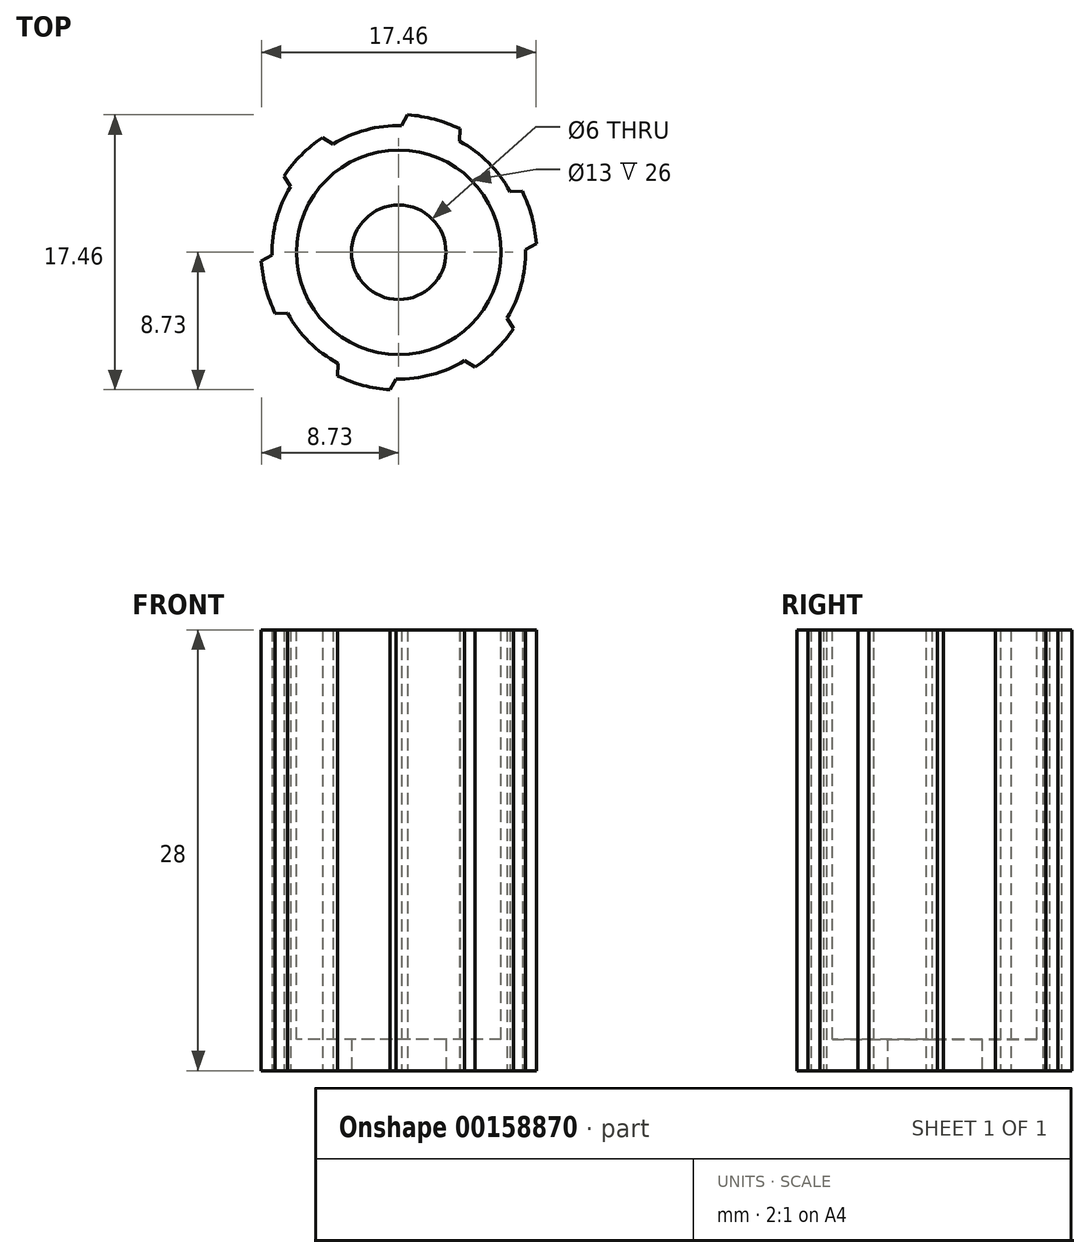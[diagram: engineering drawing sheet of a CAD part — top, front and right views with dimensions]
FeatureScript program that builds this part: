
annotation { "Feature Type Name" : "Feature", "Feature Type Description" : "" }
export const myFeature = defineFeature(function(context is Context, id is Id, definition is map)
    precondition{}
    {
        {
            var Q0;
            Q0=qCreatedBy(makeId("Top.planeOp"),FACE);
            var sketch = newSketch(context, id + "F0", { "sketchPlane" : qUnion([Q0])});
            skArc(sketch, "E0", {"start": v(6.97, -4.03) * mm, "mid": v(7.78, -2.08) * mm, "end": v(8.05, 0) * mm});
            skCircle(sketch, "E1", {"center": v(0, 0) * mm, "radius": 3 * mm});
            skArc(sketch, "E2", {"start": v(4.37, -7.58) * mm, "mid": v(6.19, -6.19) * mm, "end": v(7.58, -4.38) * mm});
            skLineSegment(sketch, "E3", {"start": v(0, -8.75) * mm, "end": v(0, -8.05) * mm});
            skLineSegment(sketch, "E4.1.0", {"start": v(4.37, -7.58) * mm, "end": v(4.03, -6.97) * mm});
            skLineSegment(sketch, "E4.2.0", {"start": v(7.58, -4.38) * mm, "end": v(6.97, -4.03) * mm});
            skLineSegment(sketch, "E4.3.0", {"start": v(8.75, 0) * mm, "end": v(8.05, 0) * mm});
            skLineSegment(sketch, "E4.4.0", {"start": v(7.58, 4.37) * mm, "end": v(6.97, 4.02) * mm});
            skLineSegment(sketch, "E4.5.0", {"start": v(4.37, 7.58) * mm, "end": v(4.03, 6.97) * mm});
            skLineSegment(sketch, "E4.6.0", {"start": v(0, 8.75) * mm, "end": v(0, 8.05) * mm});
            skLineSegment(sketch, "E4.7.0", {"start": v(-4.37, 7.58) * mm, "end": v(-4.02, 6.97) * mm});
            skLineSegment(sketch, "E4.8.0", {"start": v(-7.58, 4.38) * mm, "end": v(-6.97, 4.03) * mm});
            skLineSegment(sketch, "E4.9.0", {"start": v(-8.75, 0) * mm, "end": v(-8.05, 0) * mm});
            skLineSegment(sketch, "E4.10.0", {"start": v(-7.58, -4.38) * mm, "end": v(-6.97, -4.03) * mm});
            skLineSegment(sketch, "E4.11.0", {"start": v(-4.38, -7.58) * mm, "end": v(-4.03, -6.97) * mm});
            skArc(sketch, "E5.trimOffspring", {"start": v(8.75, 0) * mm, "mid": v(8.45, 2.26) * mm, "end": v(7.58, 4.37) * mm});
            skArc(sketch, "E6.trimOffspring", {"start": v(6.97, 4.02) * mm, "mid": v(5.7, 5.7) * mm, "end": v(4.02, 6.97) * mm});
            skArc(sketch, "E7.trimOffspring", {"start": v(4.38, 7.58) * mm, "mid": v(2.26, 8.45) * mm, "end": v(0, 8.75) * mm});
            skArc(sketch, "E8.trimOffspring", {"start": v(0, 8.05) * mm, "mid": v(-2.08, 7.78) * mm, "end": v(-4.02, 6.97) * mm});
            skArc(sketch, "E9.trimOffspring", {"start": v(-4.37, 7.58) * mm, "mid": v(-6.19, 6.19) * mm, "end": v(-7.58, 4.38) * mm});
            skArc(sketch, "E10.trimOffspring", {"start": v(-6.97, 4.02) * mm, "mid": v(-7.78, 2.08) * mm, "end": v(-8.05, 0) * mm});
            skArc(sketch, "E11.trimOffspring", {"start": v(-8.75, 0) * mm, "mid": v(-8.45, -2.26) * mm, "end": v(-7.58, -4.37) * mm});
            skArc(sketch, "E12.trimOffspring", {"start": v(-6.97, -4.03) * mm, "mid": v(-5.7, -5.7) * mm, "end": v(-4.03, -6.97) * mm});
            skArc(sketch, "E13.trimOffspring", {"start": v(-4.37, -7.58) * mm, "mid": v(-2.26, -8.45) * mm, "end": v(0, -8.75) * mm});
            skArc(sketch, "E14.trimOffspring", {"start": v(0, -8.05) * mm, "mid": v(2.08, -7.78) * mm, "end": v(4.02, -6.97) * mm});
            skSolve(sketch);
        }
        {
            var Q0;
            Q0 = qSketchRegion(id + "F0", true);
            extrude(context, id + "F1", {"entities" : qUnion([Q0]), "depth" : 28 * mm});
        }
        {
            var Q0;
            Q0=makeQuery(id+"F1.opExtrude","CAP_FACE",FACE,{"disambiguationData":[OSD([sQuery(id+"F0.wireOp",EDGE,"E0")])],"isStart":false});
            var sketch = newSketch(context, id + "F2", { "sketchPlane" : qUnion([Q0])});
            skCircle(sketch, "E15", {"center": v(0, 0) * mm, "radius": 6.5 * mm});
            skSolve(sketch);
        }
        {
            var Q0;
            Q0 = qSketchRegion(id + "F2", true);
            extrude(context, id + "F3", {"entities" : qUnion([Q0]), "operationType" : NewBodyOperationType.REMOVE, "oppositeDirection" : true, "depth" : 26 * mm});
        }
        {
            var Q0;
            Q0=makeQuery(id+"F1.opExtrude","SWEPT_EDGE",EDGE,{"disambiguationData":[OSD([sQuery(id+"F0.wireOp",EDGE,"E4.10.0"),sQuery(id+"F0.wireOp",EDGE,"E11.trimOffspring")])]});
            var Q1;
            Q1=makeQuery(id+"F1.opExtrude","SWEPT_EDGE",EDGE,{"disambiguationData":[OSD([sQuery(id+"F0.wireOp",EDGE,"E3"),sQuery(id+"F0.wireOp",EDGE,"E13.trimOffspring")])]});
            var Q2;
            Q2=makeQuery(id+"F1.opExtrude","SWEPT_EDGE",EDGE,{"disambiguationData":[OSD([sQuery(id+"F0.wireOp",EDGE,"E2"),sQuery(id+"F0.wireOp",EDGE,"E4.2.0")])]});
            var Q3;
            Q3=makeQuery(id+"F1.opExtrude","SWEPT_EDGE",EDGE,{"disambiguationData":[OSD([sQuery(id+"F0.wireOp",EDGE,"E4.4.0"),sQuery(id+"F0.wireOp",EDGE,"E5.trimOffspring")])]});
            var Q4;
            Q4=makeQuery(id+"F1.opExtrude","SWEPT_EDGE",EDGE,{"disambiguationData":[OSD([sQuery(id+"F0.wireOp",EDGE,"E4.6.0"),sQuery(id+"F0.wireOp",EDGE,"E7.trimOffspring")])]});
            var Q5;
            Q5=makeQuery(id+"F1.opExtrude","SWEPT_EDGE",EDGE,{"disambiguationData":[OSD([sQuery(id+"F0.wireOp",EDGE,"E4.8.0"),sQuery(id+"F0.wireOp",EDGE,"E9.trimOffspring")])]});
            chamfer(context, id + "F4", {"entities" : qUnion([Q0, Q1, Q2, Q3, Q4, Q5]), "chamferType" : ChamferType.TWO_OFFSETS, "width1" : 1 * mm, "oppositeDirection" : false, "width2" : 0.5 * mm, "tangentPropagation" : true});
        }
        {
            var Q0;
            Q0=makeQuery(id+"F1.opExtrude","SWEPT_EDGE",EDGE,{"disambiguationData":[OSD([sQuery(id+"F0.wireOp",EDGE,"E4.9.0"),sQuery(id+"F0.wireOp",EDGE,"E11.trimOffspring")])]});
            var Q1;
            Q1=makeQuery(id+"F1.opExtrude","SWEPT_EDGE",EDGE,{"disambiguationData":[OSD([sQuery(id+"F0.wireOp",EDGE,"E4.7.0"),sQuery(id+"F0.wireOp",EDGE,"E9.trimOffspring")])]});
            var Q2;
            Q2=makeQuery(id+"F1.opExtrude","SWEPT_EDGE",EDGE,{"disambiguationData":[OSD([sQuery(id+"F0.wireOp",EDGE,"E4.5.0"),sQuery(id+"F0.wireOp",EDGE,"E7.trimOffspring")])]});
            var Q3;
            Q3=makeQuery(id+"F1.opExtrude","SWEPT_EDGE",EDGE,{"disambiguationData":[OSD([sQuery(id+"F0.wireOp",EDGE,"E4.3.0"),sQuery(id+"F0.wireOp",EDGE,"E5.trimOffspring")])]});
            var Q4;
            Q4=makeQuery(id+"F1.opExtrude","SWEPT_EDGE",EDGE,{"disambiguationData":[OSD([sQuery(id+"F0.wireOp",EDGE,"E2"),sQuery(id+"F0.wireOp",EDGE,"E4.1.0")])]});
            var Q5;
            Q5=makeQuery(id+"F1.opExtrude","SWEPT_EDGE",EDGE,{"disambiguationData":[OSD([sQuery(id+"F0.wireOp",EDGE,"E4.11.0"),sQuery(id+"F0.wireOp",EDGE,"E13.trimOffspring")])]});
            chamfer(context, id + "F5", {"entities" : qUnion([Q0, Q1, Q2, Q3, Q4, Q5]), "chamferType" : ChamferType.TWO_OFFSETS, "width1" : 0.5 * mm, "oppositeDirection" : false, "width2" : 1 * mm, "tangentPropagation" : true});
        }
    });
